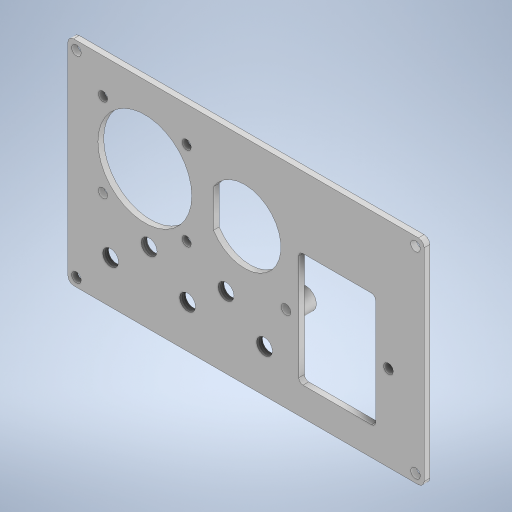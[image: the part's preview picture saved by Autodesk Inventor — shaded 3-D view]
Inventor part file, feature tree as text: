
AUTODESK INVENTOR PART (.ipt)
format: ipt  version: 2023 (Build 270158000, 158)  size: 336,896 bytes
history: native  units: in
note: dims shown in document units (in); Inventor stores cm internally (conversion verified against a paired STEP export)
features: sketch x8, extrude x5, hole x4, fillet x2, projected_geometry x1
ambient origin geometry x8: Origin, YZ Plane, XZ Plane, XY Plane, X Axis, Y Axis, Z Axis, Center Point
bodies: Solid1 (feature_tree)
feature tree (20):
  extrude  "Extrusion1"  Depth=2.9528in
  hole  "Hole1"  [1 undecoded]
  fillet  "Fillet1"  Radius=0.0787in
  extrude  "Extrusion2"  Depth=1.5748in
  fillet  "Fillet2"  Radius=0.6693in
  hole  "Hole2"  [1 undecoded]
  extrude  "Extrusion4"  Depth=0.0787in
  hole  "Hole3"  [1 undecoded]
  extrude  "Extrusion5"  Depth=1.063in
  sketch  "Sketch9"  dims[d36=0.4291in d38=0.3937in d39=0.0in d40=2.126in d43=0.5906in d45=0.22in d46=0.5in d47=0.1575in d48=0.0787in d49=90.0deg d50=0.6389in d51=0.8108in d52=0.0787in d53=0.0787in d54=0.1969in d55=0.0in d56=0.5906in d57=0.3937in d58=1.063in d59=1.2969in d60=1.063in d61=1.063in d62=1.1559in d63=1.1559in d64=0.3937in d65=0.0in d66=0.128in d67=0.2362in d68=0.1575in d69=0.0787in d70=90.0deg d71=0.315in d72=0.8108in d73=0.9843in d74=2.4409in d75=1.063in]
  extrude  "Extrusion6"  Depth=1.063in
  hole  "Hole4"  [1 undecoded]
  sketch  "Sketch1"  dims[d0=4.9213in d1=2.9528in]
  sketch  "Sketch2"  dims[d2=0.0787in d3=0.0in d4=0.1181in]
  projected_geometry  "Projected Loop1"
  sketch  "Sketch3"  dims[d5=0.1339in d6=0.2362in d7=0.248in d8=0.1409in d9=90.0deg d10=9.4488in d11=0.0in d12=0.0787in]
  sketch  "Sketch4"  dims[d13=1.063in d14=1.5748in d16=0.6693in]
  sketch  "Sketch6"  dims[d17=0.0in d18=0.0in d19=0.0591in]
  sketch  "Sketch7"  dims[d21=1.417in]
  sketch  "Sketch8"  dims[d22=0.1339in d23=0.1969in d24=0.248in d25=0.0787in d26=90.0deg d27=0.2362in d28=0.8108in d35=1.0039in]
note: 4 required parameter values undecoded (feature->parameter linkage not recoverable at this tier; creation-order binding heuristic only, values carry confidence <= 0.55)
